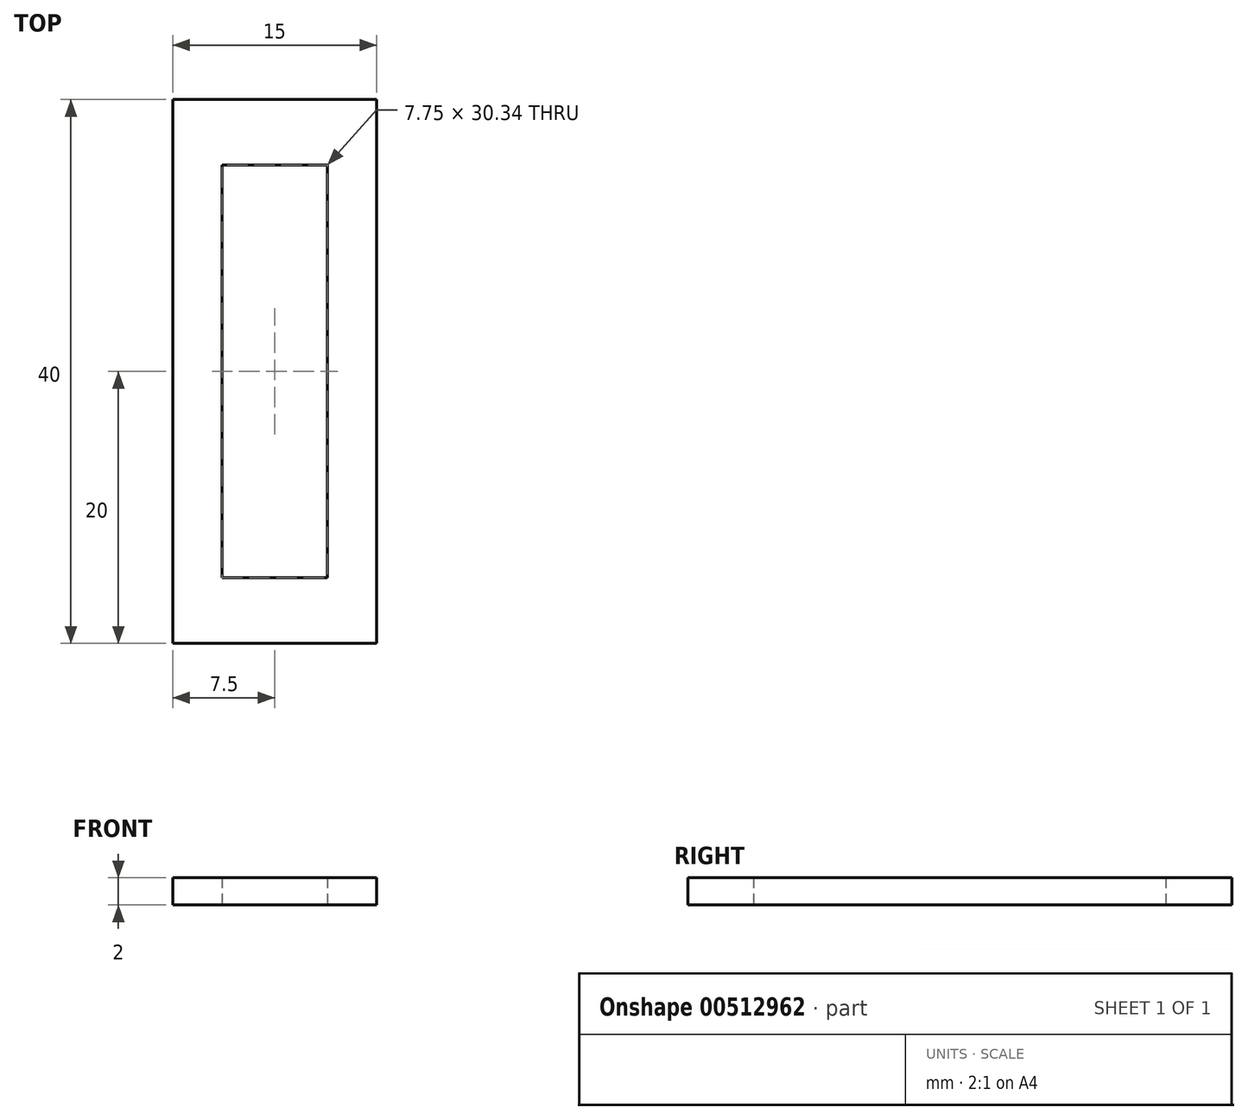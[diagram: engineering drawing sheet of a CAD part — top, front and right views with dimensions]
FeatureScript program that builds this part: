
annotation { "Feature Type Name" : "Feature", "Feature Type Description" : "" }
export const myFeature = defineFeature(function(context is Context, id is Id, definition is map)
    precondition{}
    {
        {
            var Q0;
            Q0=qCreatedBy(makeId("Top.planeOp"),FACE);
            var sketch = newSketch(context, id + "F0", { "sketchPlane" : qUnion([Q0])});
            skLineSegment(sketch, "E0.bottom", {"start": v(-7.5, 20) * mm, "end": v(7.5, 20) * mm});
            skLineSegment(sketch, "E0.top", {"start": v(-7.5, -20) * mm, "end": v(7.5, -20) * mm});
            skLineSegment(sketch, "E0.left", {"start": v(-7.5, 20) * mm, "end": v(-7.5, -20) * mm});
            skLineSegment(sketch, "E0.right", {"start": v(7.5, 20) * mm, "end": v(7.5, -20) * mm});
            skPoint(sketch, "E0.middle", {"position": v(0, 0) * mm});
            skCircle(sketch, "E1", {"center": v(0, 11.3) * mm, "radius": 3.5 * mm});
            skLineSegment(sketch, "E2.bottom", {"start": v(-3.87, 15.17) * mm, "end": v(3.87, 15.17) * mm});
            skLineSegment(sketch, "E2.top", {"start": v(-3.87, -15.17) * mm, "end": v(3.87, -15.17) * mm});
            skLineSegment(sketch, "E2.left", {"start": v(-3.87, 15.17) * mm, "end": v(-3.87, -15.17) * mm});
            skLineSegment(sketch, "E2.right", {"start": v(3.87, 15.17) * mm, "end": v(3.87, -15.17) * mm});
            skSolve(sketch);
        }
        {
            var Q0;
            Q0=makeQuery(id+"F0.imprint","IMPRINT",FACE,{"disambiguationData":[TD([[makeQuery(id+"F0.imprint","IMPRINT",EDGE,{"derivedFrom":sQuery(id+"F0.wireOp",EDGE,"E0.bottom")}),-1.0]])]});
            extrude(context, id + "F1", {"entities" : qUnion([Q0]), "depth" : 2 * mm, "offsetDistance" : 25 * mm});
        }
    });
